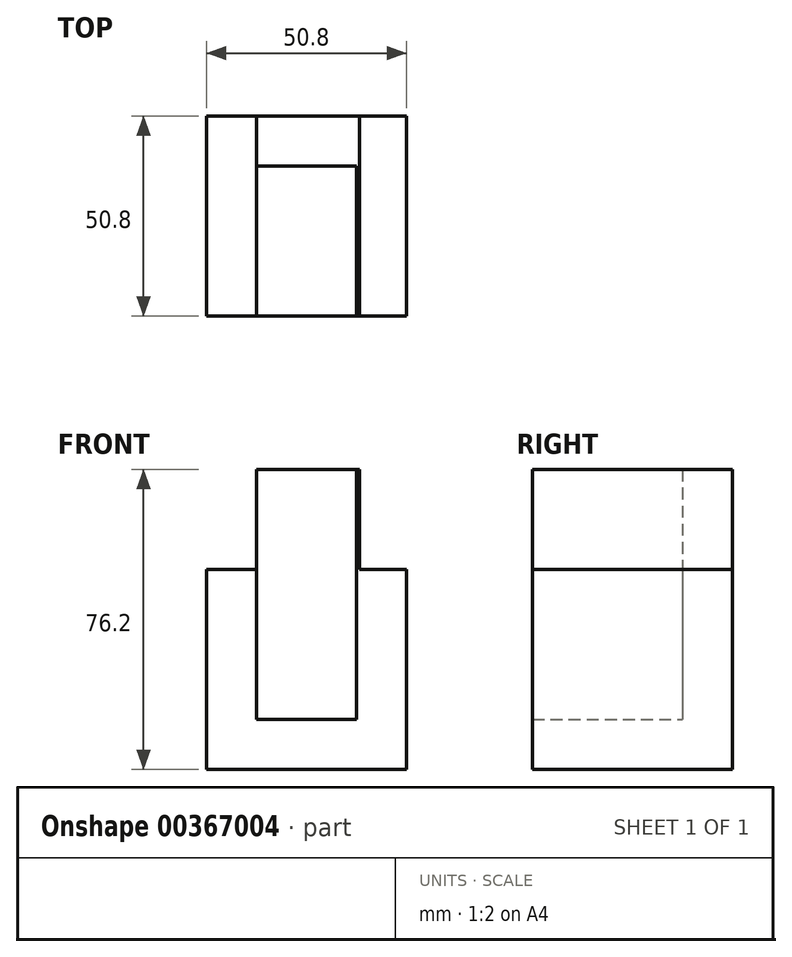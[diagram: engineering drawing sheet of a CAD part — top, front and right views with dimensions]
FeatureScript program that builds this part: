
annotation { "Feature Type Name" : "Feature", "Feature Type Description" : "" }
export const myFeature = defineFeature(function(context is Context, id is Id, definition is map)
    precondition{}
    {
        {
            var Q0;
            Q0=qCreatedBy(makeId("Front.planeOp"),FACE);
            var sketch = newSketch(context, id + "F0", { "sketchPlane" : qUnion([Q0])});
            skLineSegment(sketch, "E0.bottom", {"start": v(0, 0) * mm, "end": v(50.8, 0) * mm});
            skLineSegment(sketch, "E0.top", {"start": v(0, -76.2) * mm, "end": v(50.8, -76.2) * mm});
            skLineSegment(sketch, "E0.left", {"start": v(0, 0) * mm, "end": v(0, -76.2) * mm});
            skLineSegment(sketch, "E0.right", {"start": v(50.8, 0) * mm, "end": v(50.8, -76.2) * mm});
            skSolve(sketch);
        }
        {
            var Q0;
            Q0 = qSketchRegion(id + "F0", true);
            extrude(context, id + "F1", {"entities" : qUnion([Q0]), "depth" : 50.8 * mm});
        }
        {
            var Q0;
            Q0=makeQuery(id+"F1.opExtrude","CAP_FACE",FACE,{"disambiguationData":[OSD([sQuery(id+"F0.wireOp",EDGE,"E0.bottom"),sQuery(id+"F0.wireOp",EDGE,"E0.top"),sQuery(id+"F0.wireOp",EDGE,"E0.left"),sQuery(id+"F0.wireOp",EDGE,"E0.right")])],"isStart":false});
            var Q1;
            Q1=makeQuery(id+"F1.opExtrude","SWEPT_FACE",FACE,{"disambiguationData":[OSD([sQuery(id+"F0.wireOp",EDGE,"E0.bottom")])]});
            shell(context, id + "F2", {"entities" : qUnion([Q0, Q1]), "thickness" : 12.7 * mm});
        }
        {
            var Q0;
            Q0=qCreatedBy(makeId("Front.planeOp"),FACE);
            var sketch = newSketch(context, id + "F3", { "sketchPlane" : qUnion([Q0])});
            skLineSegment(sketch, "E1.bottom", {"start": v(0, 0) * mm, "end": v(12.7, 0) * mm});
            skLineSegment(sketch, "E1.top", {"start": v(0, -25.4) * mm, "end": v(12.7, -25.4) * mm});
            skLineSegment(sketch, "E1.left", {"start": v(0, 0) * mm, "end": v(0, -25.4) * mm});
            skLineSegment(sketch, "E1.right", {"start": v(12.7, 0) * mm, "end": v(12.7, -25.4) * mm});
            skLineSegment(sketch, "E2.bottom", {"start": v(51.6, 0) * mm, "end": v(38.9, 0) * mm});
            skLineSegment(sketch, "E2.top", {"start": v(51.6, -25.4) * mm, "end": v(38.9, -25.4) * mm});
            skLineSegment(sketch, "E2.left", {"start": v(51.6, 0) * mm, "end": v(51.6, -25.4) * mm});
            skLineSegment(sketch, "E2.right", {"start": v(38.9, 0) * mm, "end": v(38.9, -25.4) * mm});
            skSolve(sketch);
        }
        {
            var Q0;
            Q0 = qSketchRegion(id + "F3", true);
            extrude(context, id + "F4", {"entities" : qUnion([Q0]), "operationType" : NewBodyOperationType.REMOVE, "depth" : 79.7 * mm});
        }
    });
